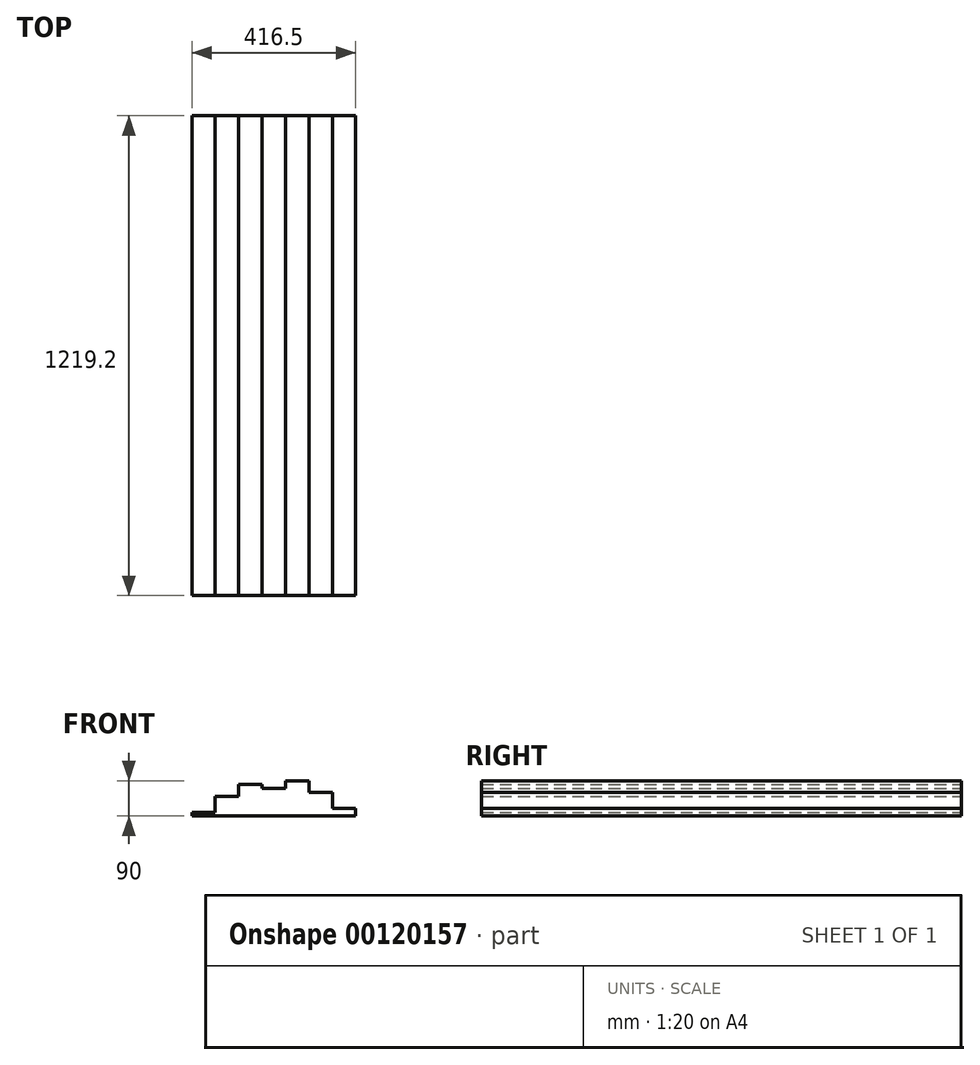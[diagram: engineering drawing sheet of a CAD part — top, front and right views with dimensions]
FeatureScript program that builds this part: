
annotation { "Feature Type Name" : "Feature", "Feature Type Description" : "" }
export const myFeature = defineFeature(function(context is Context, id is Id, definition is map)
    precondition{}
    {
        {
            var Q0;
            Q0=qCreatedBy(makeId("Front.planeOp"),FACE);
            var sketch = newSketch(context, id + "F0", { "sketchPlane" : qUnion([Q0])});
            skLineSegment(sketch, "E0", {"start": v(0, 0) * mm, "end": v(0, 10) * mm});
            skLineSegment(sketch, "E1", {"start": v(416.5, 10) * mm, "end": v(416.5, 0) * mm});
            skLineSegment(sketch, "E2", {"start": v(416.5, 0) * mm, "end": v(0, 0) * mm});
            skLineSegment(sketch, "E3", {"start": v(0, 10) * mm, "end": v(59.5, 10) * mm});
            skLineSegment(sketch, "E4", {"start": v(59.5, 10) * mm, "end": v(59.5, 50) * mm});
            skLineSegment(sketch, "E5", {"start": v(59.5, 50) * mm, "end": v(119, 50) * mm});
            skLineSegment(sketch, "E6", {"start": v(119, 50) * mm, "end": v(119, 80) * mm});
            skLineSegment(sketch, "E7", {"start": v(119, 80) * mm, "end": v(178.5, 80) * mm});
            skLineSegment(sketch, "E8", {"start": v(178.5, 80) * mm, "end": v(178.5, 70) * mm});
            skLineSegment(sketch, "E9", {"start": v(178.5, 70) * mm, "end": v(238, 70) * mm});
            skLineSegment(sketch, "E10", {"start": v(238, 70) * mm, "end": v(238, 90) * mm});
            skLineSegment(sketch, "E11", {"start": v(238, 90) * mm, "end": v(297.5, 90) * mm});
            skLineSegment(sketch, "E12", {"start": v(297.5, 90) * mm, "end": v(297.5, 60) * mm});
            skLineSegment(sketch, "E13", {"start": v(297.5, 60) * mm, "end": v(357, 60) * mm});
            skLineSegment(sketch, "E14", {"start": v(357, 60) * mm, "end": v(357, 20) * mm});
            skLineSegment(sketch, "E15", {"start": v(357, 20) * mm, "end": v(416.5, 20) * mm});
            skLineSegment(sketch, "E16", {"start": v(416.5, 20) * mm, "end": v(416.5, 10) * mm});
            skSolve(sketch);
        }
        {
            var Q0;
            Q0=makeQuery(id+"F0.imprint","IMPRINT",FACE,{"disambiguationData":[TD([[makeQuery(id+"F0.imprint","IMPRINT",EDGE,{"derivedFrom":sQuery(id+"F0.wireOp",EDGE,"E0")}),-1.0]])]});
            extrude(context, id + "F1", {"entities" : qUnion([Q0]), "depth" : 1219.2 * mm});
        }
    });
